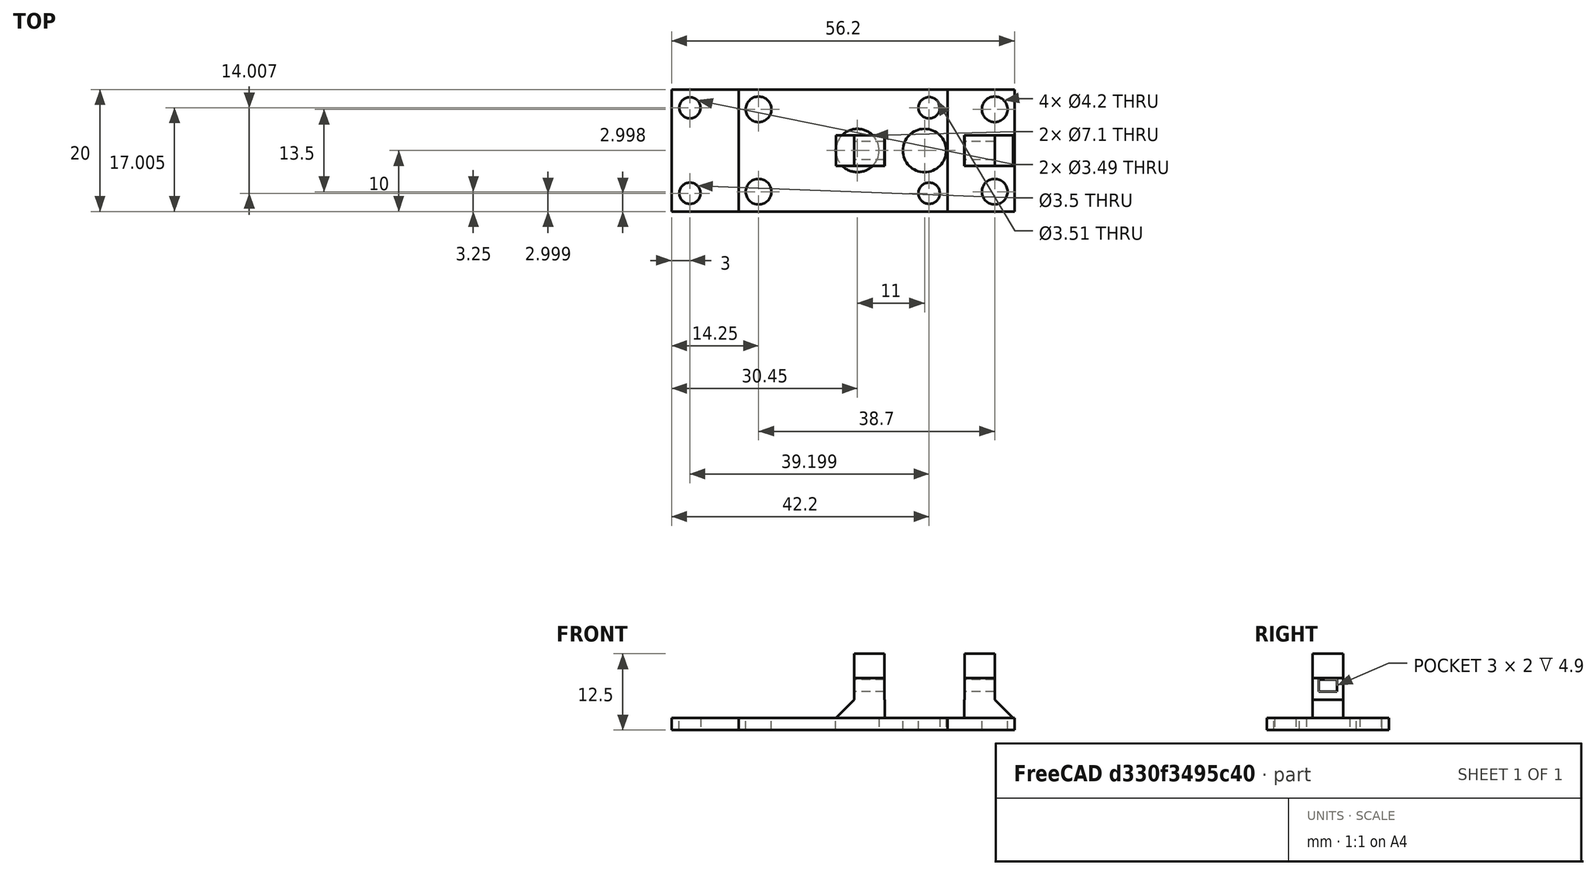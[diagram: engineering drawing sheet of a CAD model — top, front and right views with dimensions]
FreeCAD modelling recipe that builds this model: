
FCSTD DOCUMENT  (FreeCAD 0.17R13522 (Git))
Label: v5_base_inferior_con_soportes
License: CreativeCommons Attribution-ShareAlike
LicenseURL: http://creativecommons.org/licenses/by-sa/4.0/
objects: Part::Cut×12, Part::Extrusion×9, Part::Part2DObjectPython×8, Part::Fuse×8, Part::Feature×5, Part::Box×4, Part::Cylinder×4, Part::Chamfer×2
note: 52 computed .brp shape members not serialized (recipe doc carries the construction recipe); baked Part::Feature solids carry a one-line shape summary decoded from their .brp

FEATURE [Part::Box] Box  label="placa base"
  AttacherType = Attacher::AttachEngine3D
  Height = 2
  Length = 45.2
  Width = 20
FEATURE [Part::Part2DObjectPython] Circle  label="taladro inferior izquierdo"  # Draft 2D object (typed FeaturePython)
  FirstAngle = 0
  LastAngle = 0
  MakeFace = false
  Placement = pos=(3,2.99873,2) rot=(0,0,1;3.14159rad)
  Radius = 1.74945
FEATURE [Part::Part2DObjectPython] Circle001  label="taladro inferior derecho"  # Draft 2D object (typed FeaturePython)
  FirstAngle = 0
  LastAngle = 0
  MakeFace = false
  Placement = pos=(42.1991,2.99781,2) rot=(0,0,1;3.14159rad)
  Radius = 1.7464
FEATURE [Part::Part2DObjectPython] Circle002  label="taladro superior derecho"  # Draft 2D object (typed FeaturePython)
  FirstAngle = 0
  LastAngle = 0
  MakeFace = false
  Placement = pos=(42.2,17.005,2) rot=(0,0,1;3.14159rad)
  Radius = 1.75369
FEATURE [Part::Part2DObjectPython] Circle003  label="taladro superior izquierdo"  # Draft 2D object (typed FeaturePython)
  FirstAngle = 0
  LastAngle = 0
  MakeFace = false
  Placement = pos=(3,17.005,2) rot=(0,0,1;3.14159rad)
  Radius = 1.74699
FEATURE [Part::Extrusion] Extrude
  Base = -> Circle003
  Dir = (0,0,1)
  DirMode = 2
  FaceMakerClass = Part::FaceMakerBullseye
  LengthFwd = 10
  LengthRev = 0
  Placement = pos=(0,0,-5) rot=(0,0,1;0rad)
  Solid = true
  Symmetric = false
FEATURE [Part::Extrusion] Extrude001
  Base = -> Circle
  Dir = (0,0,1)
  DirMode = 2
  FaceMakerClass = Part::FaceMakerBullseye
  LengthFwd = 10
  LengthRev = 0
  Placement = pos=(0,0,-5) rot=(0,0,1;0rad)
  Solid = true
  Symmetric = false
FEATURE [Part::Extrusion] Extrude002
  Base = -> Circle001
  Dir = (0,0,1)
  DirMode = 2
  FaceMakerClass = Part::FaceMakerBullseye
  LengthFwd = 10
  LengthRev = 0
  Placement = pos=(0,0,-5) rot=(0,0,1;0rad)
  Solid = true
  Symmetric = false
FEATURE [Part::Extrusion] Extrude003
  Base = -> Circle002
  Dir = (0,0,1)
  DirMode = 2
  FaceMakerClass = Part::FaceMakerBullseye
  LengthFwd = 10
  LengthRev = 0
  Placement = pos=(0,0,-5) rot=(0,0,1;0rad)
  Solid = true
  Symmetric = false
FEATURE [Part::Cut] Cut
  Base = -> Box
  Refine = true
  Tool = -> Extrude001
FEATURE [Part::Cut] Cut001
  Base = -> Cut
  Refine = true
  Tool = -> Extrude
FEATURE [Part::Part2DObjectPython] Circle004  # Draft 2D object (typed FeaturePython)
  FirstAngle = 0
  LastAngle = 0
  MakeFace = false
  Placement = pos=(30.45,10,2) rot=(0,0,1;3.14159rad)
  Radius = 3.55
FEATURE [Part::Extrusion] Extrude004
  Base = -> Circle004
  Dir = (0,0,1)
  DirMode = 2
  FaceMakerClass = Part::FaceMakerBullseye
  LengthFwd = 10
  LengthRev = 0
  Placement = pos=(0,0,-4) rot=(0,0,1;0rad)
  Solid = true
  Symmetric = false
FEATURE [Part::Cut] Cut002
  Base = -> Cut001
  Refine = true
  Tool = -> Extrude002
FEATURE [Part::Cut] Cut003  label="base con taladros en esquina"
  Base = -> Cut002
  Refine = true
  Tool = -> Extrude003
FEATURE [Part::Feature] Clone002_solid  label="Clone002 (Solid)"
  Placement = pos=(22.6,40,0) rot=(0,0,1;0rad)
  shape: bbox 6 x 5 x 8 mm, 10 faces (baked)
FEATURE [Part::Feature] Clone001001  label="Clone003"
  Placement = pos=(38.3,10,0) rot=(0,0,1;0rad)
  shape: bbox 6 x 5 x 8 mm, 10 faces (baked)
FEATURE [Part::Feature] Cut004_solid001001  label="base con agujeros (Solid)002"
  shape: bbox 45.2 x 20 x 2 mm, 11 faces (baked)
FEATURE [Part::Fuse] Fusion
  Base = -> Clone002_solid
  Refine = true
  Tool = -> Cut004_solid001001
FEATURE [Part::Chamfer] Chamfer
  Base = -> Fusion
  Edges = 1 edges r=3: [Edge24]
FEATURE [Part::Fuse] Fusion001
  Base = -> Clone001001
  Refine = true
  Tool = -> Chamfer
FEATURE [Part::Chamfer] Chamfer001
  Base = -> Fusion001
  Edges = 1 edges r=3: [Edge24]
FEATURE [Part::Box] Box001  label="Cube"
  AttacherType = Attacher::AttachEngine3D
  Height = 10
  Length = 6
  Placement = pos=(31,6,5) rot=(0,0,1;0rad)
  Width = 15
FEATURE [Part::Feature] Box001001  label="Cube001"
  Placement = pos=(23.9,5,5) rot=(0,0,1;0rad)
  shape: bbox 6 x 15 x 10 mm, 6 faces (baked)
FEATURE [Part::Cut] Cut005
  Base = -> Chamfer001
  Refine = true
  Tool = -> Box001
FEATURE [Part::Cut] Cut006
  Base = -> Cut005
  Refine = true
  Tool = -> Box001001
FEATURE [Part::Part2DObjectPython] Rectangle002  # Draft 2D object (typed FeaturePython)
  ChamferSize = 0
  Columns = 1
  FilletRadius = 0
  Height = 4.95
  Length = 5
  MakeFace = true
  Placement = pos=(18.95,12.5,8.5001) rot=(0,0,-1;1.5708rad)
  Rows = 1
FEATURE [Part::Extrusion] Extrude005
  Base = -> Rectangle002
  Dir = (0,0,1)
  DirMode = 2
  FaceMakerClass = Part::FaceMakerBullseye
  LengthFwd = 4
  LengthRev = 0
  Solid = false
  Symmetric = false
FEATURE [Part::Extrusion] Extrude006
  Base = -> Rectangle002
  Dir = (0,0,1)
  DirMode = 2
  FaceMakerClass = Part::FaceMakerBullseye
  LengthFwd = 4
  LengthRev = 0
  Solid = false
  Symmetric = false
FEATURE [Part::Fuse] Fusion002
  Base = -> Cut006
  Refine = true
  Tool = -> Extrude005
FEATURE [Part::Fuse] Fusion003
  Base = -> Extrude006
  Refine = true
  Tool = -> Fusion002
FEATURE [Part::Part2DObjectPython] Rectangle003  # Draft 2D object (typed FeaturePython)
  ChamferSize = 0
  Columns = 1
  FilletRadius = 0
  Height = 4.95
  Length = 5
  MakeFace = true
  Placement = pos=(37,12.5,8.5001) rot=(0,0,-1;1.5708rad)
  Rows = 1
FEATURE [Part::Extrusion] Extrude007
  Base = -> Rectangle003
  Dir = (0,0,1)
  DirMode = 2
  FaceMakerClass = Part::FaceMakerBullseye
  LengthFwd = 4
  LengthRev = 0
  Solid = false
  Symmetric = false
FEATURE [Part::Extrusion] Extrude008
  Base = -> Rectangle003
  Dir = (0,0,1)
  DirMode = 2
  FaceMakerClass = Part::FaceMakerBullseye
  LengthFwd = 4
  LengthRev = 0
  Solid = false
  Symmetric = false
FEATURE [Part::Fuse] Fusion004
  Base = -> Fusion003
  Refine = true
  Tool = -> Extrude008
FEATURE [Part::Fuse] Fusion005
  Base = -> Extrude007
  Placement = pos=(3,0,0) rot=(0,0,1;0rad)
  Refine = true
  Tool = -> Fusion004
FEATURE [Part::Feature] Extrude009001  label="Extrude010"
  Placement = pos=(3,0,0) rot=(0,0,1;0rad)
  shape: bbox 36 x 3 x 2 mm, 6 faces (baked)
FEATURE [Part::Cut] Cut007
  Base = -> Fusion005
  Placement = pos=(8,0,0) rot=(0,0,1;0rad)
  Refine = true
  Tool = -> Extrude009001
FEATURE [Part::Part2DObjectPython] Rectangle  # Draft 2D object (typed FeaturePython)
  ChamferSize = 0
  Columns = 1
  FilletRadius = 0
  Height = 1.8
  Length = 2.8
  MakeFace = true
  Placement = pos=(56.2,27.001,2.00104) rot=(0.57735,-0.57735,0.57735;4.18879rad)
  Rows = 1
FEATURE [Part::Cut] Cut004  label="base con agujeros"
  Base = -> Cut003
  Refine = true
  Tool = -> Extrude004
FEATURE [Part::Cylinder] Cylinder
  Angle = 360
  AttacherType = Attacher::AttachEngine3D
  Height = 10
  Placement = pos=(14.25,16.75,-5) rot=(0,0,1;0rad)
  Radius = 2.1
FEATURE [Part::Cylinder] Cylinder001
  Angle = 360
  AttacherType = Attacher::AttachEngine3D
  Height = 10
  Placement = pos=(14.25,3.25,-4) rot=(0,0,1;0rad)
  Radius = 2.1
FEATURE [Part::Cylinder] Cylinder002
  Angle = 360
  AttacherType = Attacher::AttachEngine3D
  Height = 10
  Placement = pos=(52.95,3.25,-5) rot=(0,0,1;0rad)
  Radius = 2.1
FEATURE [Part::Cylinder] Cylinder003
  Angle = 360
  AttacherType = Attacher::AttachEngine3D
  Height = 10
  Placement = pos=(52.95,16.75,-4) rot=(0,0,1;0rad)
  Radius = 2.1
FEATURE [Part::Box] Box001002  label="Cube002"
  AttacherType = Attacher::AttachEngine3D
  Height = 2
  Length = 11
  Placement = pos=(11,0,0) rot=(0,0,1;0rad)
  Width = 20
FEATURE [Part::Fuse] Fusion006
  Base = -> Cut007
  Refine = true
  Tool = -> Box001002
FEATURE [Part::Cut] Cut008
  Base = -> Fusion006
  Refine = true
  Tool = -> Cylinder001
FEATURE [Part::Cut] Cut009
  Base = -> Cut008
  Refine = true
  Tool = -> Cylinder
FEATURE [Part::Box] Box001003  label="Cube003"
  AttacherType = Attacher::AttachEngine3D
  Height = 2
  Length = 10
  Placement = pos=(46,0,0) rot=(0,0,1;0rad)
  Width = 20
FEATURE [Part::Fuse] Fusion007
  Base = -> Cut009
  Refine = true
  Tool = -> Box001003
FEATURE [Part::Cut] Cut010
  Base = -> Fusion007
  Refine = true
  Tool = -> Cylinder002
FEATURE [Part::Cut] Cut011
  Base = -> Cut010
  Refine = true
  Tool = -> Cylinder003
